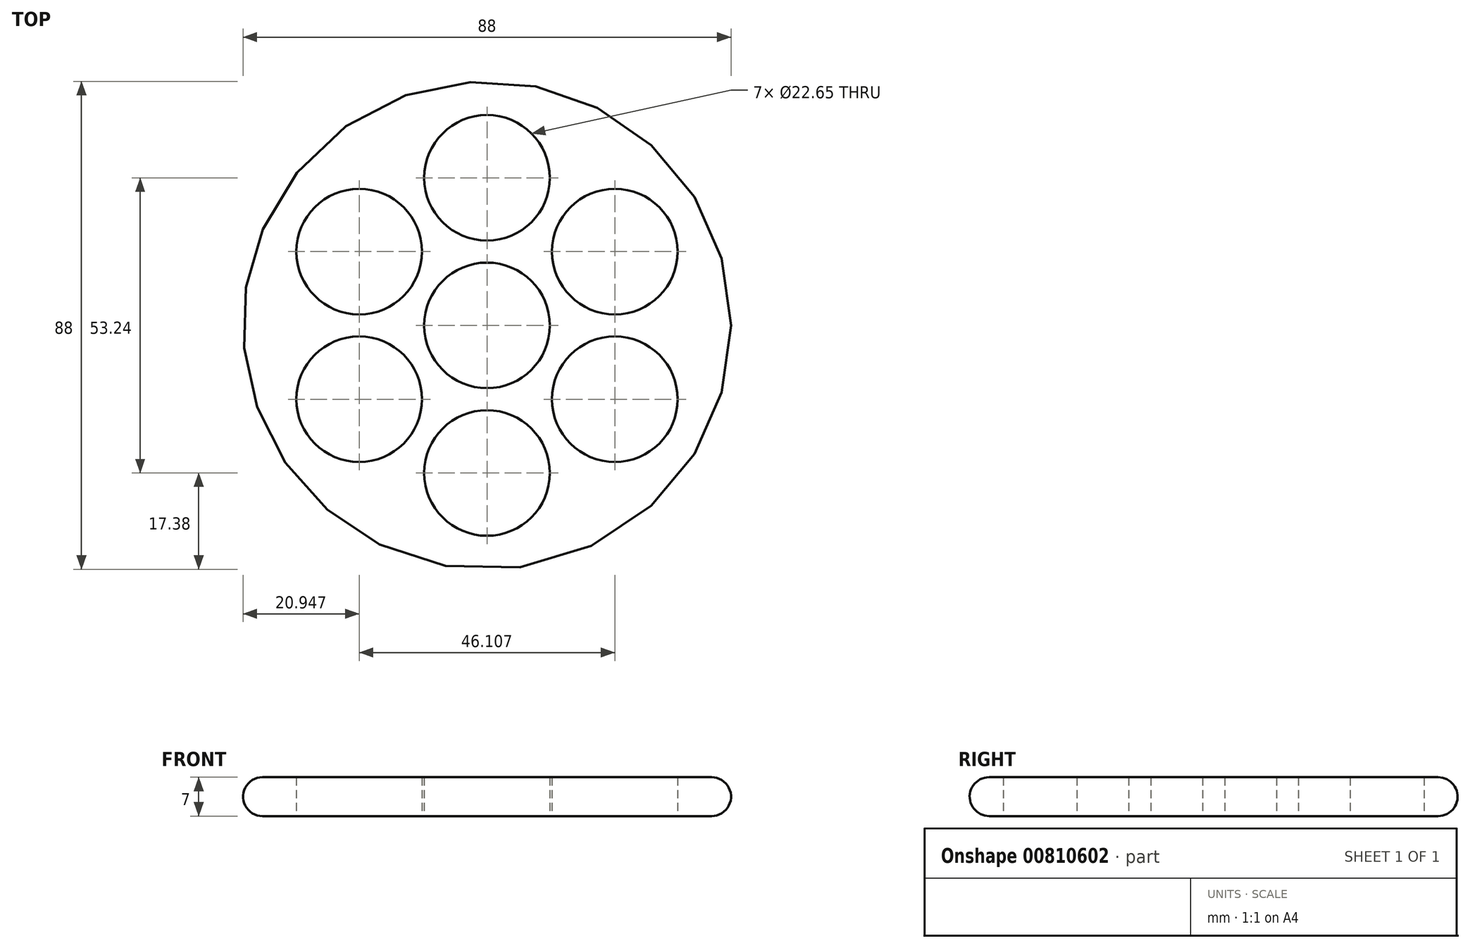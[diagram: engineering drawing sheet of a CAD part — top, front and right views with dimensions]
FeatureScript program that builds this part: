
annotation { "Feature Type Name" : "Feature", "Feature Type Description" : "" }
export const myFeature = defineFeature(function(context is Context, id is Id, definition is map)
    precondition{}
    {
        {
            var Q0;
            Q0=qCreatedBy(makeId("Top.planeOp"),FACE);
            var sketch = newSketch(context, id + "F0", { "sketchPlane" : qUnion([Q0])});
            skCircle(sketch, "E0", {"center": v(0, 0) * mm, "radius": 11.33 * mm});
            skCircle(sketch, "E1", {"center": v(0, 26.62) * mm, "radius": 11.32 * mm});
            skCircle(sketch, "E2.1.0", {"center": v(-23.05, 13.3) * mm, "radius": 11.32 * mm});
            skCircle(sketch, "E2.2.0", {"center": v(-23.05, -13.3) * mm, "radius": 11.32 * mm});
            skCircle(sketch, "E3", {"center": v(0, 0) * mm, "radius": 44 * mm});
            skCircle(sketch, "E4.1.3.0", {"center": v(0, -26.62) * mm, "radius": 11.32 * mm});
            skCircle(sketch, "E4.1.4.0", {"center": v(23.05, -13.3) * mm, "radius": 11.32 * mm});
            skCircle(sketch, "E4.1.5.0", {"center": v(23.05, 13.3) * mm, "radius": 11.32 * mm});
            skSolve(sketch);
        }
        {
            var Q0;
            Q0=makeQuery(id+"F0.imprint","IMPRINT",FACE,{"disambiguationData":[TD([[makeQuery(id+"F0.imprint","IMPRINT",EDGE,{"derivedFrom":sQuery(id+"F0.wireOp",EDGE,"E0")}),-1.0]])]});
            extrude(context, id + "F1", {"entities" : qUnion([Q0]), "depth" : 7 * mm, "offsetDistance" : 25 * mm});
        }
        {
            var Q0;
            Q0=makeQuery(id+"F1.opExtrude","CAP_EDGE",EDGE,{"disambiguationData":[OSD([sQuery(id+"F0.wireOp",EDGE,"E3")])],"isStart":false});
            fillet(context, id + "F2", {"entities" : qUnion([Q0]), "radius" : 3.5 * mm, "tangentPropagation" : true, "allowEdgeOverflow" : false});
        }
        {
            var Q0;
            Q0=makeQuery(id+"F1.opExtrude","CAP_EDGE",EDGE,{"disambiguationData":[OSD([sQuery(id+"F0.wireOp",EDGE,"E3")])],"isStart":true});
            fillet(context, id + "F3", {"entities" : qUnion([Q0]), "radius" : 3.5 * mm, "tangentPropagation" : true, "allowEdgeOverflow" : false});
        }
    });
